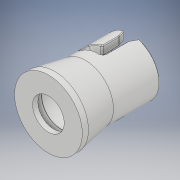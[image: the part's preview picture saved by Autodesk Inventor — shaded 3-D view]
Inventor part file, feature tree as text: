
AUTODESK INVENTOR PART (.ipt)
format: ipt  version: 2019 (Build 230136000, 136)  size: 1,601,536 bytes
history: native  units: mm
features: other x3, extrude x1, sketch x1
ambient origin geometry x8: Origin, YZ Plane, XZ Plane, XY Plane, X Axis, Y Axis, Z Axis, Center Point
bodies: Solide1 (feature_tree)
feature tree (5):
  other  "reservoir.ipt"
  extrude  "Extrusion1"  Depth=10.0mm
  other  "Solide1::reservoir.ipt"
  other  "FonctionRepérage1"
  sketch  "Esquisse1"
